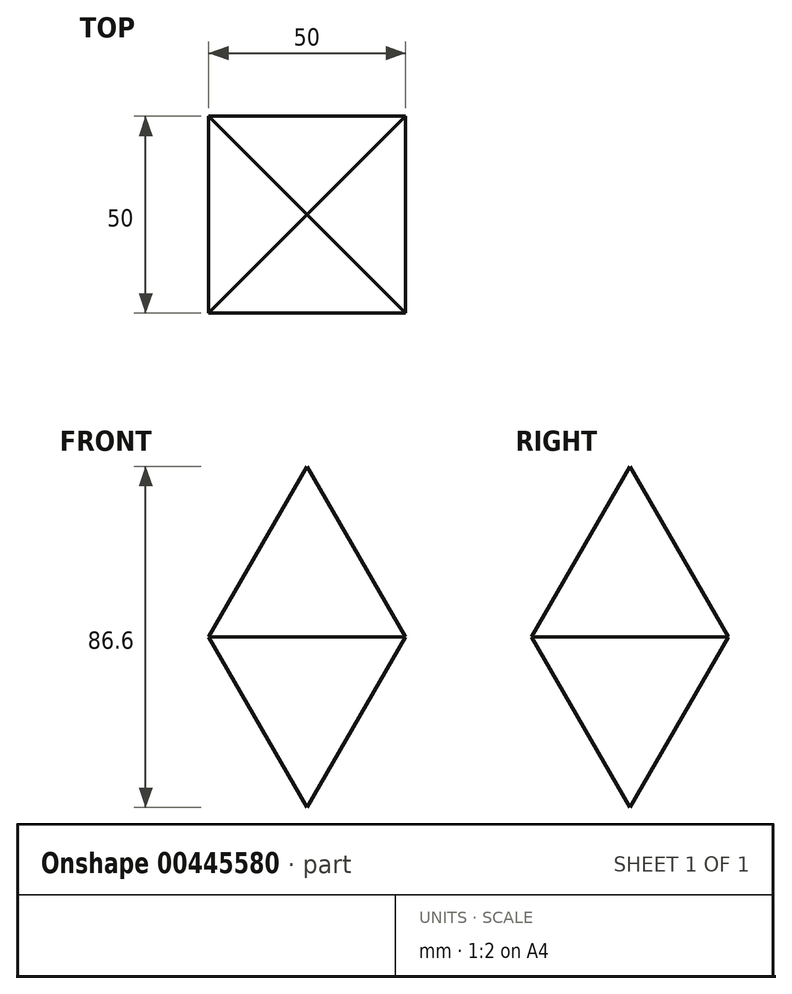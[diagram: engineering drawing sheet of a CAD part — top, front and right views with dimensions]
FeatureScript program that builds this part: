
annotation { "Feature Type Name" : "Feature", "Feature Type Description" : "" }
export const myFeature = defineFeature(function(context is Context, id is Id, definition is map)
    precondition{}
    {
        {
            var Q0;
            Q0=qCreatedBy(makeId("Top.planeOp"),FACE);
            var sketch = newSketch(context, id + "F0", { "sketchPlane" : qUnion([Q0])});
            skLineSegment(sketch, "E0.bottom", {"start": v(25, -25) * mm, "end": v(-25, -25) * mm});
            skLineSegment(sketch, "E0.top", {"start": v(25, 25) * mm, "end": v(-25, 25) * mm});
            skLineSegment(sketch, "E0.left", {"start": v(25, -25) * mm, "end": v(25, 25) * mm});
            skLineSegment(sketch, "E0.right", {"start": v(-25, -25) * mm, "end": v(-25, 25) * mm});
            skPoint(sketch, "E0.middle", {"position": v(0, 0) * mm});
            skSolve(sketch);
        }
        {
            var Q0;
            Q0=qSketchRegion(id+"F0",true);
            extrude(context, id + "F1", {"entities" : qUnion([Q0]), "depth" : 50 * mm, "hasDraft" : true, "draftAngle" : 30 * degree, "draftPullDirection" : true});
        }
        {
            var Q0;
            Q0=makeQuery(id+"F1.opExtrude","SWEPT_BODY",BODY,{"disambiguationData":[OSD([sQuery(id+"F0.wireOp",EDGE,"E0.bottom"),sQuery(id+"F0.wireOp",EDGE,"E0.top"),sQuery(id+"F0.wireOp",EDGE,"E0.left"),sQuery(id+"F0.wireOp",EDGE,"E0.right")])]});
            var Q1;
            Q1=qCreatedBy(makeId("Top.planeOp"),FACE);
            mirror(context, id + "F2", {"operationType" : NewBodyOperationType.ADD, "entities" : qUnion([Q0]), "mirrorPlane" : qUnion([Q1])});
        }
    });
